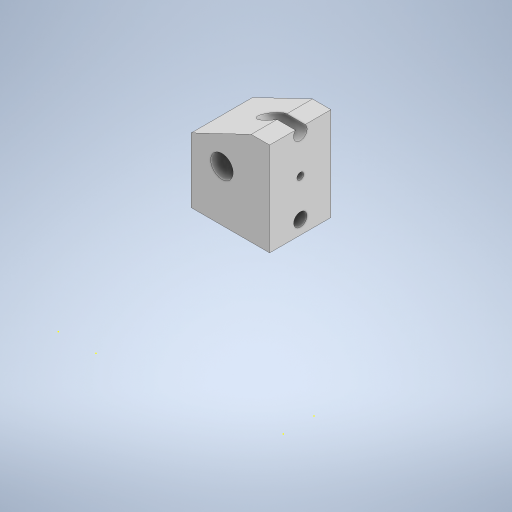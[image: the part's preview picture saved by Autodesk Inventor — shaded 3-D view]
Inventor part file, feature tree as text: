
AUTODESK INVENTOR PART (.ipt)
format: ipt  version: 2024 (Build 280153000, 153)  size: 555,520 bytes
history: native  units: mm
features: sketch x28, extrude x21, move_body x4, chamfer x3, plane x3, split x3, boolean_combine x2, other x1, fillet x1, imported_body x1
ambient origin geometry x8: Origin, YZ Plane, XZ Plane, XY Plane, X Axis, Y Axis, Z Axis, Center Point
bodies: Solid1 (feature_tree), Solid2 (feature_tree), Solid3 (feature_tree), Solid4 (feature_tree), Solid5 (feature_tree), Solid6 (feature_tree), Solid7 (feature_tree), Solid8 (feature_tree)
feature tree (67):
  other  "Repaired Geometry1"
  extrude  "Extrusion1"  Depth=16.0mm
  sketch  "Sketch2"  dims[d2=15.0mm d3=0.0mm d4=10.0mm]
  extrude  "Extrusion2"  Depth=10.0mm
  chamfer  "Chamfer1"  Distance=21.25mm
  extrude  "Extrusion3"  Depth=10.0mm TaperAngle=0.0deg
  extrude  "Extrusion4"  Depth=11.5mm TaperAngle=0.0deg
  extrude  "Extrusion5"  Depth=1.0mm TaperAngle=0.0deg
  chamfer  "Chamfer2"  Distance=6.0mm Angle=45.0deg
  sketch  "Sketch6"  dims[d14=7.0mm d15=11.5mm d16=0.0mm]
  extrude  "Extrusion6"  Depth=9.0mm
  extrude  "Extrusion7"  Depth=11.5mm TaperAngle=0.0deg
  chamfer  "Chamfer3"  Distance=11.5mm Angle=45.0deg
  sketch  "Sketch9"  dims[d26=3.3mm d27=45.25mm d28=0.0mm d29=11.5mm d30=5.5mm d31=45.0deg]
  extrude  "Extrusion8"  Depth=65.75mm TaperAngle=0.0deg
  extrude  "Extrusion9"  Depth=9.0mm TaperAngle=0.0deg
  extrude  "Extrusion10"  Depth=13.0mm TaperAngle=0.0deg
  sketch  "Sketch13"  dims[d43=24.0mm d44=21.0mm d45=0.0mm]
  extrude  "Extrusion11"  Depth=21.0mm TaperAngle=0.0deg
  extrude  "Extrusion12"  TaperAngle=0.0deg  [1 undecoded]
  extrude  "Extrusion13"  Depth=6.0mm TaperAngle=0.0deg
  plane  "Work Plane1"
  split  "Split1"
  move_body  "Move Body1"
  extrude  "Extrusion14"  Depth=0.5mm TaperAngle=0.0deg
  move_body  "Move Body2"
  fillet  "Fillet1"  Radius=10.0mm
  extrude  "Extrusion15"  Depth=10.0mm TaperAngle=0.0deg
  sketch  "Sketch19"  dims[d71=29.5mm d72=0.0mm d73=13.75mm]
  sketch  "Sketch20"  dims[d74=26.0mm d75=0.0mm d76=-5.0mm d77=0.0mm d78=0.0mm]
  extrude  "Extrusion16"  Depth=1.0mm
  extrude  "Extrusion18"  Depth=29.5mm
  extrude  "Extrusion19"  TaperAngle=0.0deg  [1 undecoded]
  sketch  "Sketch23"  dims[d83=1.0mm d84=1.0mm d85=0.0mm]
  sketch  "Sketch24"
  extrude  "Extrusion20"  TaperAngle=0.0deg  [1 undecoded]
  plane  "Work Plane2"
  boolean_combine  "Combine1"
  split  "Split2"
  extrude  "Extrusion21"  Depth=1.0mm TaperAngle=0.0deg
  move_body  "Move Body3"
  boolean_combine  "Combine2"
  plane  "Work Plane3"
  split  "Split3"
  move_body  "Move Body4"
  extrude  "Extrusion22"  [1 undecoded]
  sketch  "Sketch28"
  sketch  "Sketch29"
  sketch  "Sketch1"  dims[d0=36.0mm d1=16.0mm]
  sketch  "Sketch3"  dims[d5=10.0mm]
  sketch  "Sketch4"  dims[d6=3.3mm d7=21.25mm d8=0.0mm]
  sketch  "Sketch5"  dims[d9=10.0mm d10=5.5mm d11=45.0deg d12=10.0mm d13=0.0mm]
  sketch  "Sketch7"  dims[d17=3.3mm d18=1.0mm d19=0.0mm d20=6.0mm d21=11.5mm d22=45.0deg]
  sketch  "Sketch8"  dims[d23=15.0mm d24=0.0mm d25=9.0mm]
  sketch  "Sketch10"  dims[d32=2.0mm d33=65.75mm d34=0.0mm]
  sketch  "Sketch11"  dims[d35=0.5mm d36=0.0mm d37=9.0mm d38=0.0mm]
  sketch  "Sketch12"  dims[d39=0.5mm d40=0.0mm d41=13.0mm d42=0.0mm]
  sketch  "Sketch14"  dims[d46=12.25mm d47=-12.0mm d48=0.0mm d49=0.0mm]
  sketch  "Sketch15"  dims[d50=30.0mm d51=0.0mm d52=6.0mm d53=0.0mm d54=0.0mm d55=4.0mm]
  sketch  "Sketch16"  dims[d56=0.5mm d57=0.0mm d58=0.5mm d59=0.0mm d64=10.0mm d65=0.0mm]
  sketch  "Sketch17"  dims[d66=3.0mm d67=10.0mm d68=0.0mm]
  sketch  "Sketch18"  dims[d69=1.0mm d70=31.0mm]
  sketch  "Sketch22"  dims[d79=0.0mm d80=0.0mm d81=0.0mm d82=-30.0mm]
  sketch  "Sketch25"
  sketch  "Sketch26"
  imported_body  "Base1"
  sketch  "Sketch27"
note: 4 required parameter values undecoded (feature->parameter linkage not recoverable at this tier; creation-order binding heuristic only, values carry confidence <= 0.55)
